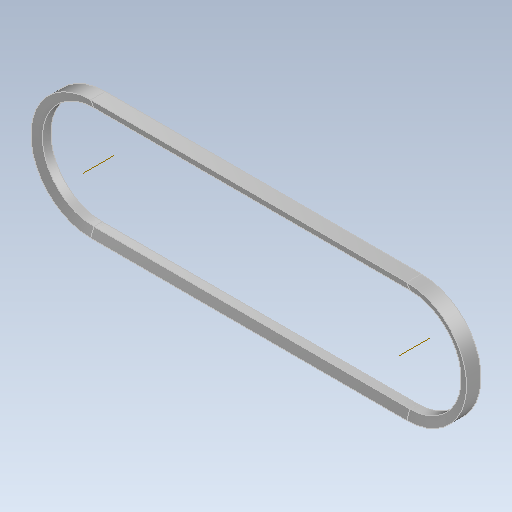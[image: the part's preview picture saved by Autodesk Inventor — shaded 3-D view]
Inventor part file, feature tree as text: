
AUTODESK INVENTOR PART (.ipt)
format: ipt  version: 2021 (Build 250183000, 183)  size: 108,544 bytes
history: native  units: mm (DEFAULTED — no unit token found)
features: other x4, sketch x1, sweep x1
ambient origin geometry x8: Origin, YZ Plane, XZ Plane, XY Plane, X Axis, Y Axis, Z Axis, Center Point
bodies: Solid1 (feature_tree)
feature tree (6):
  sketch  "Sketch Path"  dims[d0=8.5mm d1=2.498591mm d2=6.981317mm d3=6.0mm d4=0.0mm d5=0.0mm d6=0.0mm d7=0.0mm d8=0.0mm d9=0.0mm]
  other  "Cross Section Plane"
  other  "Work Axis1"
  other  "Work Axis2"
  sweep  "Belt"
  other  "Cross Section"
